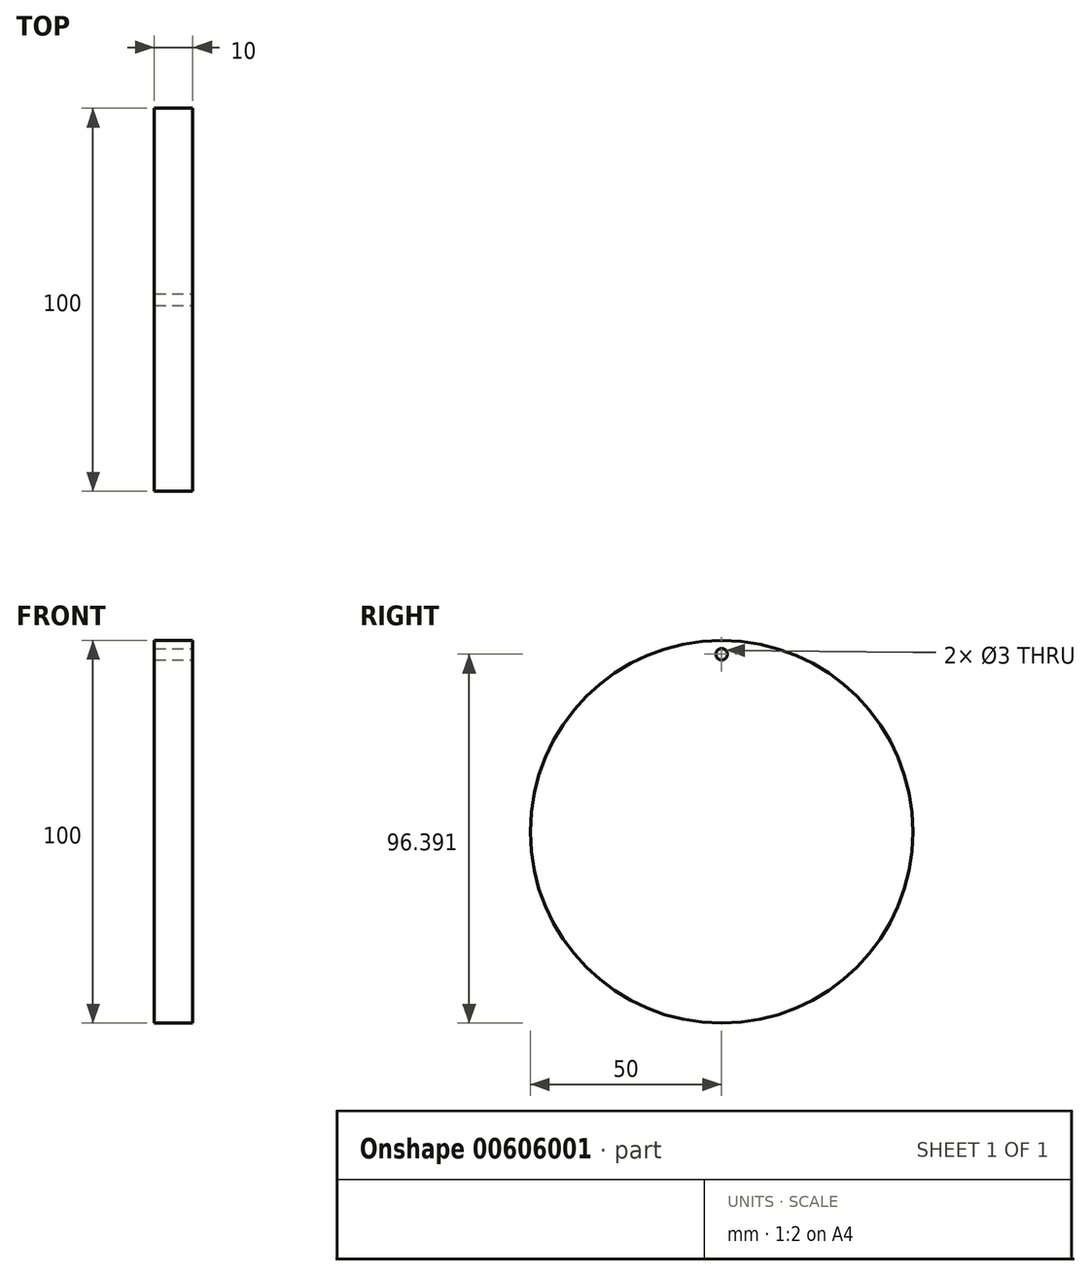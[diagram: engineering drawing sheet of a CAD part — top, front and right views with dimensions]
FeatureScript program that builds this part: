
annotation { "Feature Type Name" : "Feature", "Feature Type Description" : "" }
export const myFeature = defineFeature(function(context is Context, id is Id, definition is map)
    precondition{}
    {
        {
            var Q0;
            Q0=qCreatedBy(makeId("Right.planeOp"),FACE);
            var sketch = newSketch(context, id + "F0", { "sketchPlane" : qUnion([Q0])});
            skCircle(sketch, "E0", {"center": v(0, 0) * mm, "radius": 50 * mm});
            skSolve(sketch);
        }
        {
            var Q0;
            Q0=makeQuery(id+"F0.imprint","IMPRINT",FACE,{"disambiguationData":[TD([[makeQuery(id+"F0.imprint","IMPRINT",EDGE,{"derivedFrom":sQuery(id+"F0.wireOp",EDGE,"E0")}),1.0]])]});
            extrude(context, id + "F1", {"entities" : qUnion([Q0]), "endBound" : BoundingType.SYMMETRIC, "depth" : 10 * mm, "offsetDistance" : 25 * mm});
        }
        {
            var Q0;
            Q0=makeQuery(id+"F1.opExtrude","CAP_FACE",FACE,{"disambiguationData":[OSD([sQuery(id+"F0.wireOp",EDGE,"E0")])],"isStart":false});
            var sketch = newSketch(context, id + "F2", { "sketchPlane" : qUnion([Q0])});
            skCircle(sketch, "E1", {"center": v(0, 46.4) * mm, "radius": 2.07 * mm});
            skSolve(sketch);
        }
        {
            var Q0;
            Q0=sQuery(id+"F2.wireOp",VERTEX,"E1.center");
            var Q1;
            Q1=makeQuery(id+"F1.opExtrude","SWEPT_BODY",BODY,{"disambiguationData":[OSD([sQuery(id+"F0.wireOp",EDGE,"E0")])]});
            hole(context, id + "F3", {"style" : HoleStyle.SIMPLE, "endStyle" : HoleEndStyle.THROUGH, "holeDiameter" : 3 * mm, "majorDiameter" : 5 * mm, "isTappedThrough" : true, "tappedDepth" : 12 * mm, "tapClearance" : 3, "locations" : qUnion([Q0]), "scope" : qUnion([Q1])});
        }
    });
